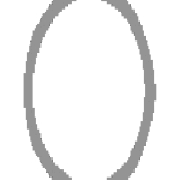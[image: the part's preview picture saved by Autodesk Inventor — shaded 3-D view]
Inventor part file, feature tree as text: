
AUTODESK INVENTOR PART (.ipt)
format: ipt  version: 2021 (Build 250183000, 183)  size: 112,640 bytes
history: native  units: in
note: dims shown in document units (in); Inventor stores cm internally (conversion verified against a paired STEP export)
features: other x4, sketch x3, plane x1
ambient origin geometry x8: Origin, YZ Plane, XZ Plane, XY Plane, X Axis, Y Axis, Z Axis, Center Point
bodies: Solid1 (feature_tree), Body (feature_tree)
feature tree (8):
  other  "Driven Length"
  other  "Frame Generator"
  other  "Start Plane"
  other  "End Plane"
  sketch  "Sketch"  dims[d2=15.5in d4=-0.0in d5=15.5in d6=0.12in d7=0.0in d8=90.0deg d9=15.5in]
  sketch  "Sketch2"  dims[d0=1.0in]
  plane  "Work Plane3"
  sketch  "Sketch3"  dims[d1=0.065in]
